# Revit family: Konsole 45- 60 Platte längs
name_source: partatom
category: HLS-Bauteile
revit_build: Autodesk Revit 2017 (Build: 20190507_1515(x64)
units: mm (PartAtom-declared; Revit-internal decimal feet)

## family parameters
Basisbauteil = Fläche
Beim Laden mit Abzugskörper schneiden = Nein
Bemaßung runder Anschluss = Durchmesser verwenden
Gemeinsam genutzt = Ja
Raumberechnungspunkt = Nein
Teiletyp = Normal

## types (4) — shared parameters
Ausrichtung Platte = längs
Breite Platte = 55 mm  [stored 0.180446 ft]
Breite Profil = 45 mm  [stored 0.147638 ft]
Fabrikat = MEFA
Firma = MEFA Befestigungs- und Montagesysteme GmbH
Höhe Profil = 60 mm  [stored 0.19685 ft]
Kurztext1 = Konsole C-Profil 45/60
Langloch Platte = 14x20 mm
Lochabstand = 100 mm
Lochdurchmesser = 14 mm
Länge Platte = 138 mm  [stored 0.452756 ft]
Material = Stahl
Materialname C-Profil = S235JR
Materialname Platte = S235JR
Oberflaeche = galvanisch verzinkt
Profil = C-Profil
Stärke Platte = 12 mm  [stored 0.0393701 ft]
Stärke Profil = 3 mm  [stored 0.00984252 ft]
Vorgabe-Ansicht = 1219 mm

## per-type parameters (varying)
| type | Artikelnummer | EAN | Gewicht | Gewicht pro Bauteil | Kurztext2 | Länge Konsole | Schienenlänge | max. zul. Last F1 | max. zul. Last F2 | max. zul. Last q0 |
| Konsole 45- 60 L= 840 Platte längs gvz | 18050840 | 4250928437679 | 4.08 kg | 4.08 kg | L= 840 mm Platte längs gvz | 840 mm  [stored 2.75591 ft] | Montageschiene 45- 60-3,0 für Konsole : C-Profil 45- 60-3,0 L=  840 | 0.61 kip | 0.25 kip | 0.222 kip/ft |
| Konsole 45- 60 L= 735 Platte längs gvz | 18050735 | 4250928437662 | 3.65 kg | 3.65 kg | L= 735 mm Platte längs gvz | 735 mm  [stored 2.41142 ft] | Montageschiene 45- 60-3,0 für Konsole : C-Profil 45- 60-3,0 L=  735 | 0.70 kip | 0.33 kip | 0.291 kip/ft |
| Konsole 45- 60 L= 630 Platte längs gvz | 18050630 | 4250928437655 | 3.23 kg | 3.23 kg | L= 630 mm Platte längs gvz | 630 mm  [stored 2.06693 ft] | Montageschiene 45- 60-3,0 für Konsole : C-Profil 45- 60-3,0 L=  630 | 0.82 kip | 0.41 kip | 0.395 kip/ft |
| Konsole 45- 60 L= 525 Platte längs gvz | 18050525 | 4250928437648 | 2.80 kg | 2.80 kg | L= 525 mm Platte längs gvz | 525 mm | Montageschiene 45- 60-3,0 für Konsole : C-Profil 45- 60-3,0 L=  525 | 0.98 kip | 0.49 kip | 0.569 kip/ft |

note: [stored X ft] marks values corroborated as IEEE doubles in the binary element streams (Revit-internal decimal feet)
